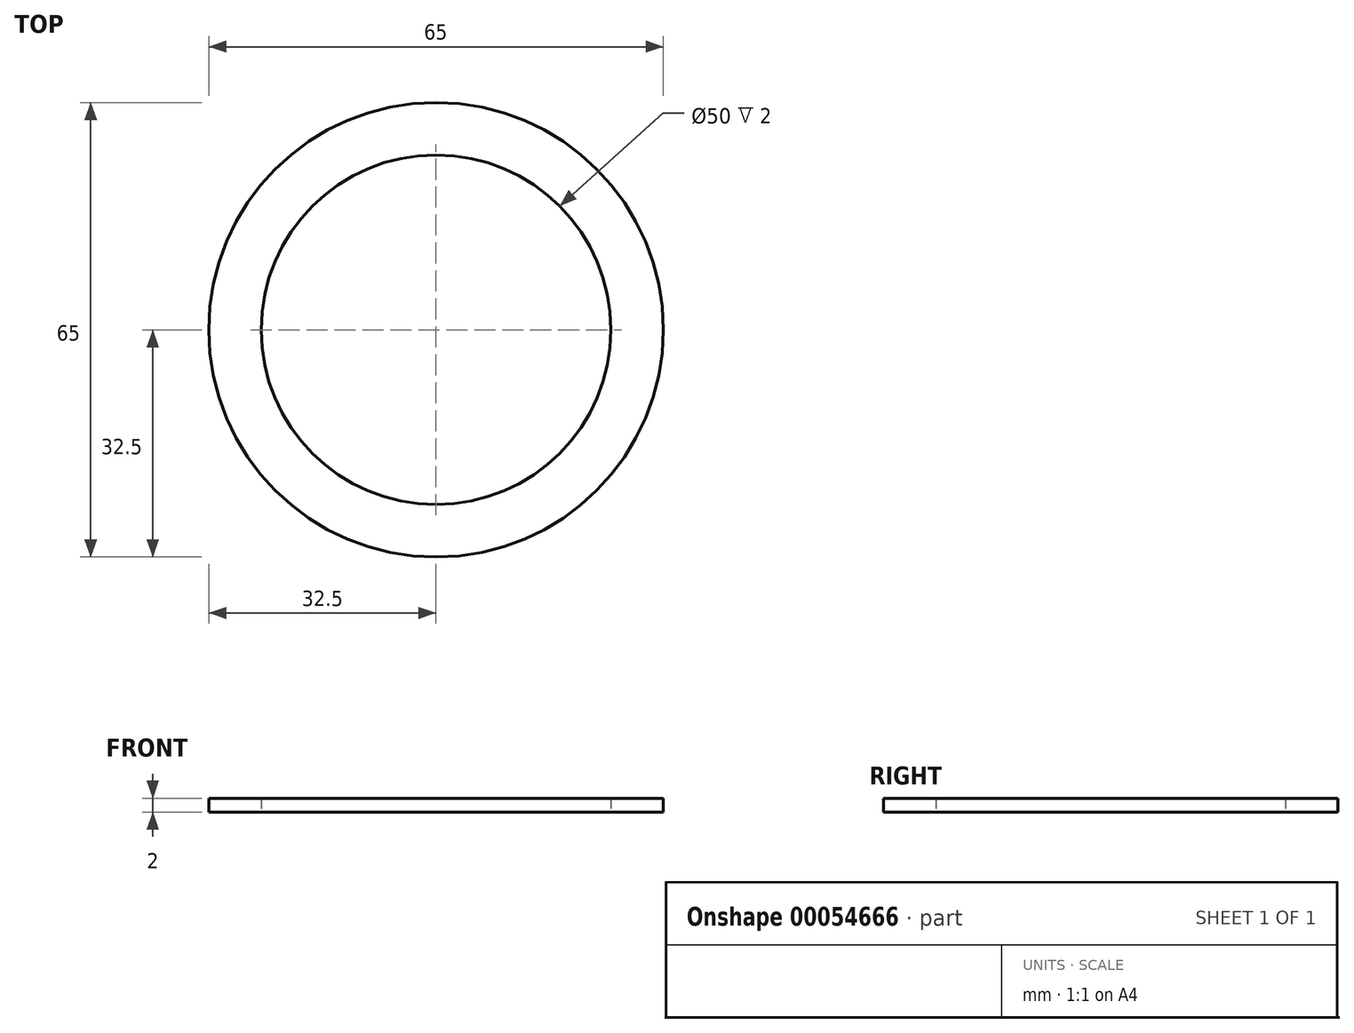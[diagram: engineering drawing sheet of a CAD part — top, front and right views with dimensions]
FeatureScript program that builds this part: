
annotation { "Feature Type Name" : "Feature", "Feature Type Description" : "" }
export const myFeature = defineFeature(function(context is Context, id is Id, definition is map)
    precondition{}
    {
        {
            var Q0;
            Q0=qCreatedBy(makeId("Top.planeOp"),FACE);
            var sketch = newSketch(context, id + "F0", { "sketchPlane" : qUnion([Q0])});
            skCircle(sketch, "E0", {"center": v(0, 0) * mm, "radius": 32.5 * mm});
            skCircle(sketch, "E1", {"center": v(0, 0) * mm, "radius": 25 * mm});
            skSolve(sketch);
        }
        {
            var Q0;
            Q0=makeQuery(id+"F0.imprint","IMPRINT",FACE,{"disambiguationData":[TD([[makeQuery(id+"F0.imprint","IMPRINT",EDGE,{"derivedFrom":sQuery(id+"F0.wireOp",EDGE,"E0")}),1.0]])]});
            extrude(context, id + "F1", {"entities" : qUnion([Q0]), "depth" : 2 * mm});
        }
    });
